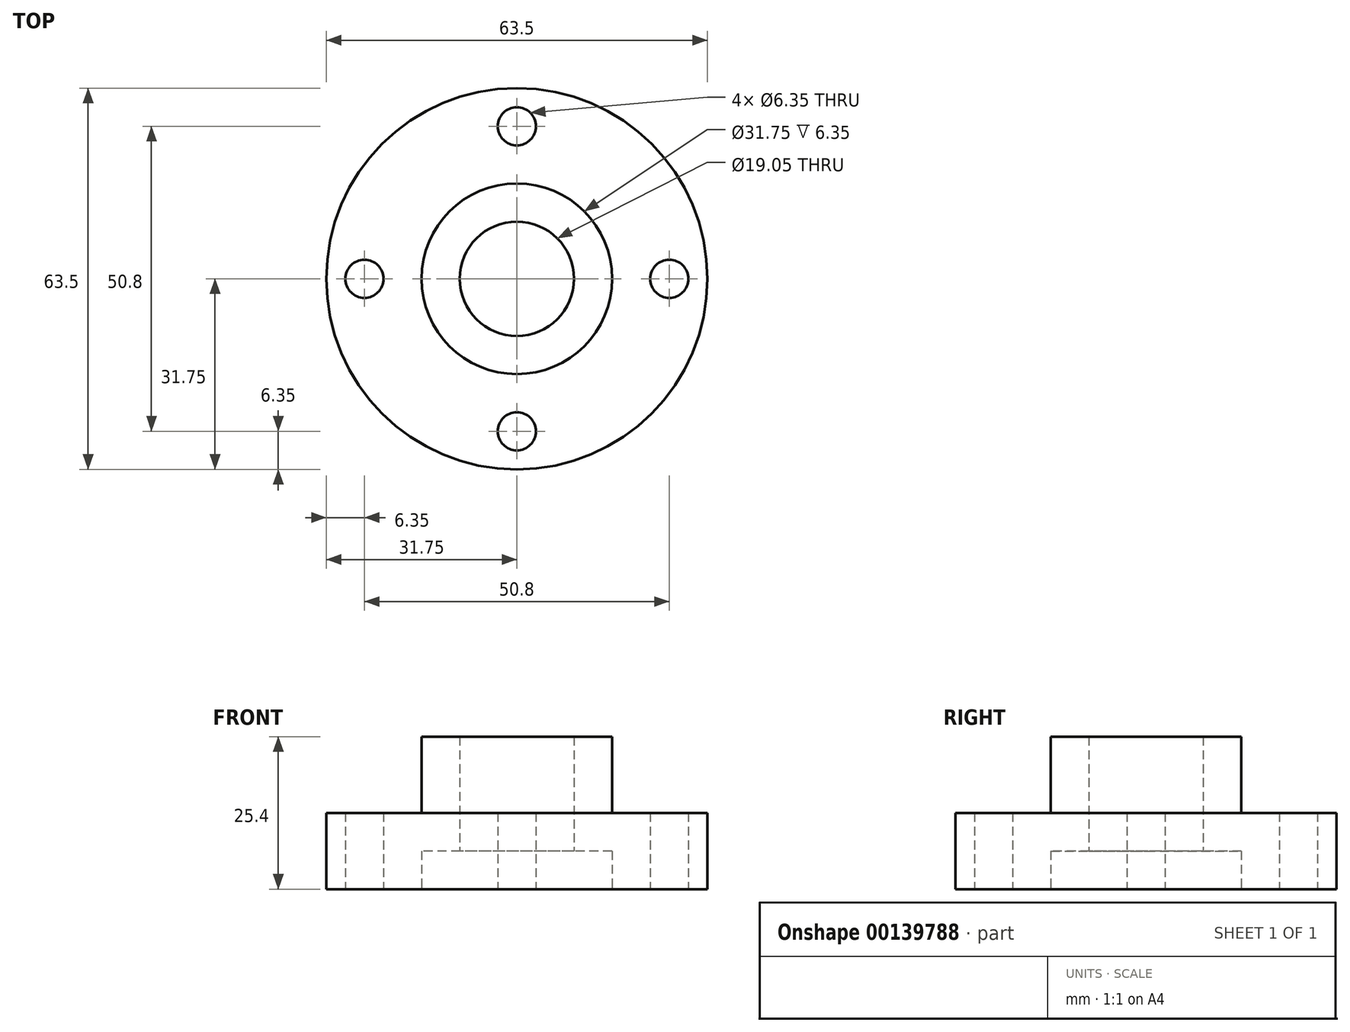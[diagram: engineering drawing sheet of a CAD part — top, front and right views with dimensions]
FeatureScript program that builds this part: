
annotation { "Feature Type Name" : "Feature", "Feature Type Description" : "" }
export const myFeature = defineFeature(function(context is Context, id is Id, definition is map)
    precondition{}
    {
        {
            var Q0;
            Q0=qCreatedBy(makeId("Top.planeOp"),FACE);
            var sketch = newSketch(context, id + "F0", { "sketchPlane" : qUnion([Q0])});
            skCircle(sketch, "E0", {"center": v(0, 0) * mm, "radius": 31.75 * mm});
            skCircle(sketch, "E1", {"center": v(0, 0) * mm, "radius": 15.88 * mm});
            skCircle(sketch, "E2", {"center": v(0, 0) * mm, "radius": 9.53 * mm});
            skCircle(sketch, "E3", {"center": v(0, 25.4) * mm, "radius": 3.18 * mm});
            skCircle(sketch, "E4", {"center": v(25.4, 0) * mm, "radius": 3.18 * mm});
            skCircle(sketch, "E5", {"center": v(0, -25.4) * mm, "radius": 3.18 * mm});
            skCircle(sketch, "E6", {"center": v(-25.4, 0) * mm, "radius": 3.18 * mm});
            skSolve(sketch);
        }
        {
            var Q0;
            Q0=makeQuery(id+"F0.imprint","IMPRINT",FACE,{"disambiguationData":[TD([[makeQuery(id+"F0.imprint","IMPRINT",EDGE,{"derivedFrom":sQuery(id+"F0.wireOp",EDGE,"E0")}),1.0]])]});
            extrude(context, id + "F1", {"entities" : qUnion([Q0]), "endBound" : BoundingType.SYMMETRIC, "depth" : 12.7 * mm});
        }
        {
            var Q0;
            Q0=makeQuery(id+"F0.imprint","IMPRINT",FACE,{"disambiguationData":[TD([[makeQuery(id+"F0.imprint","IMPRINT",EDGE,{"derivedFrom":sQuery(id+"F0.wireOp",EDGE,"E1")}),1.0]])]});
            extrude(context, id + "F2", {"entities" : qUnion([Q0]), "operationType" : NewBodyOperationType.ADD, "depth" : 19.05 * mm});
        }
    });
